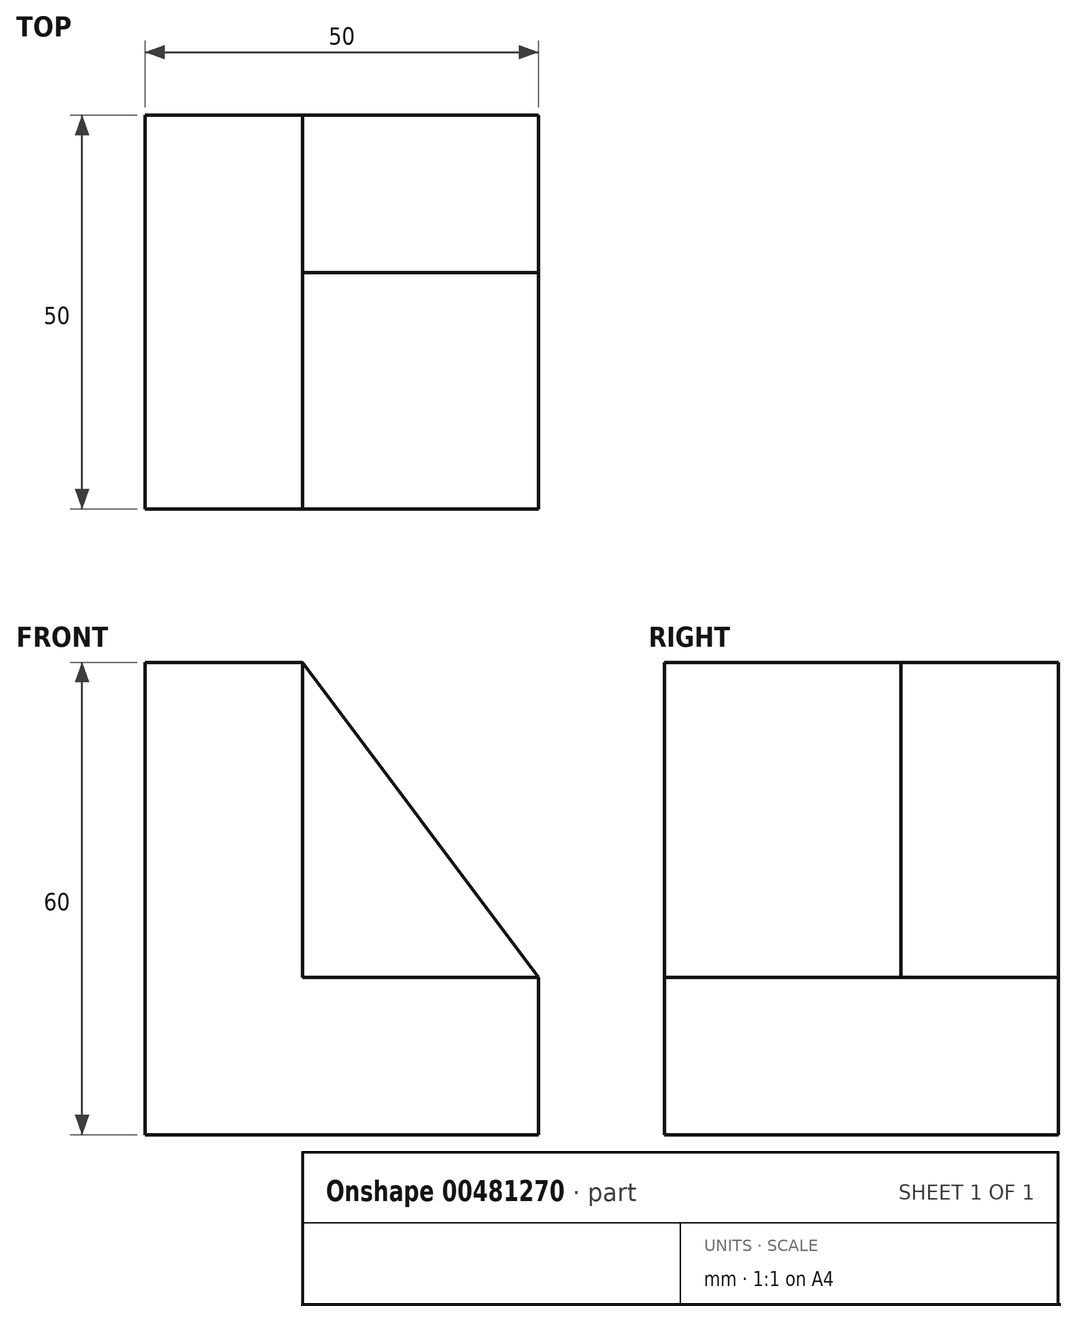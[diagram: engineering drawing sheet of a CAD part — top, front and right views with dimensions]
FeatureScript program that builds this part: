
annotation { "Feature Type Name" : "Feature", "Feature Type Description" : "" }
export const myFeature = defineFeature(function(context is Context, id is Id, definition is map)
    precondition{}
    {
        {
            var Q0;
            Q0=qCreatedBy(makeId("Front.planeOp"),FACE);
            var sketch = newSketch(context, id + "F0", { "sketchPlane" : qUnion([Q0])});
            skLineSegment(sketch, "E0", {"start": v(0, 0) * mm, "end": v(50, 0) * mm});
            skLineSegment(sketch, "E1", {"start": v(50, 0) * mm, "end": v(50, 20) * mm});
            skLineSegment(sketch, "E2", {"start": v(50, 20) * mm, "end": v(20, 20) * mm});
            skLineSegment(sketch, "E3", {"start": v(20, 20) * mm, "end": v(20, 60) * mm});
            skLineSegment(sketch, "E4", {"start": v(20, 60) * mm, "end": v(0, 60) * mm});
            skLineSegment(sketch, "E5", {"start": v(0, 60) * mm, "end": v(0, 0) * mm});
            skSolve(sketch);
        }
        {
            var Q0;
            Q0=qSketchRegion(id+"F0",true);
            extrude(context, id + "F1", {"entities" : qUnion([Q0]), "depth" : 50 * mm});
        }
        {
            var Q0;
            Q0=makeQuery(id+"F1.opExtrude","CAP_FACE",FACE,{"disambiguationData":[OSD([sQuery(id+"F0.wireOp",EDGE,"E0"),sQuery(id+"F0.wireOp",EDGE,"E1"),sQuery(id+"F0.wireOp",EDGE,"E2"),sQuery(id+"F0.wireOp",EDGE,"E3"),sQuery(id+"F0.wireOp",EDGE,"E4"),sQuery(id+"F0.wireOp",EDGE,"E5")])],"isStart":true});
            var sketch = newSketch(context, id + "F2", { "sketchPlane" : qUnion([Q0])});
            skLineSegment(sketch, "E6", {"start": v(-20, 60) * mm, "end": v(-50, 20) * mm});
            skLineSegment(sketch, "E7", {"start": v(-50, 20) * mm, "end": v(-20, 20) * mm});
            skLineSegment(sketch, "E8", {"start": v(-20, 20) * mm, "end": v(-20, 60) * mm});
            skSolve(sketch);
        }
        {
            var Q0;
            Q0 = qSketchRegion(id + "F2", true);
            extrude(context, id + "F3", {"entities" : qUnion([Q0]), "operationType" : NewBodyOperationType.ADD, "oppositeDirection" : true, "depth" : 20 * mm});
        }
    });
